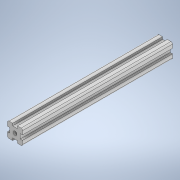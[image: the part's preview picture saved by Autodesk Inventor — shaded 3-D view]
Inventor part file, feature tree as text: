
AUTODESK INVENTOR PART (.ipt)
format: ipt  version: 2021 (Build 250183000, 183)  size: 132,608 bytes
history: native  units: mm
features: extrude x1, fillet x1, sketch x1
ambient origin geometry x8: Origin, YZ Plane, XZ Plane, XY Plane, X Axis, Y Axis, Z Axis, Center Point
bodies: Solid1 (feature_tree)
feature tree (3):
  extrude  "Extrusion1"  Depth=6.3mm
  fillet  "Fillet1"  Radius=3.0mm
  sketch  "Sketch1"  dims[d0=20.0mm d1=6.3mm d2=3.0mm d3=5.0mm d4=200.0mm d5=0.0mm d6=2.0mm]
